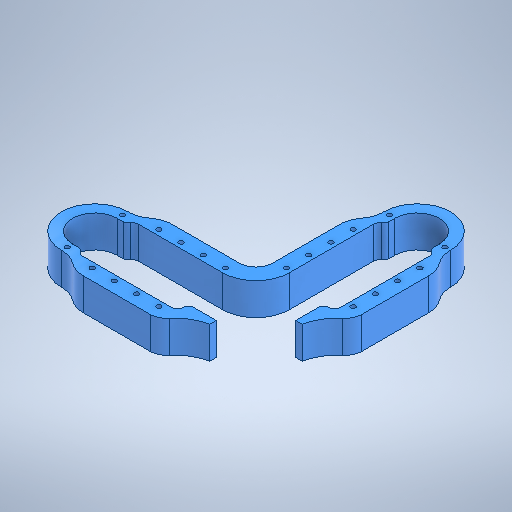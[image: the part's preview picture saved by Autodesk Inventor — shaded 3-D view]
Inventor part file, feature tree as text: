
AUTODESK INVENTOR PART (.ipt)
format: ipt  version: 2025.1 (Build 291241020, 241B)  size: 746,496 bytes
history: native  units: in
note: dims shown in document units (in); Inventor stores cm internally (conversion verified against a paired STEP export)
features: extrude x7, sketch x6, projected_geometry x5, fillet x4
ambient origin geometry x8: Origin, YZ Plane, XZ Plane, XY Plane, X Axis, Y Axis, Z Axis, Center Point
bodies: Solid1 (feature_tree)
feature tree (22):
  sketch  "Sketch1"  dims[d1=1.5in d2=1.5in d3=1.0in d4=1.0in d6=0.75in]
  extrude  "Extrusion1"  Depth=1.5in
  fillet  "Fillet1"  Radius=1.0in
  fillet  "Fillet2"  Radius=1.0in
  fillet  "Fillet4"  Radius=0.75in
  extrude  "Extrusion2"  Depth=0.75in
  fillet  "Fillet5"  Radius=1.0in
  extrude  "Extrusion3"  Depth=4.0in
  extrude  "Extrusion4"  Depth=0.75in
  extrude  "Extrusion5"  Depth=0.5in
  extrude  "Extrusion6"  Depth=0.25in
  extrude  "Extrusion7"  Depth=0.25in
  sketch  "Sketch2"  dims[d7=0.75in d8=0.75in d9=1.0in]
  projected_geometry  "Projected Loop1"
  sketch  "Sketch3"  dims[d10=4.0in d11=4.0in]
  projected_geometry  "Projected Loop2"
  sketch  "Sketch4"  dims[d17=0.75in d18=0.75in]
  projected_geometry  "Projected Loop3"
  sketch  "Sketch5"  dims[d19=0.5in d23=0.5in]
  projected_geometry  "Projected Loop4"
  sketch  "Sketch6"  dims[d24=0.75in d25=0.75in d30=0.5in d33=0.25in d47=0.75in d48=0.75in d49=0.5in d50=0.5in d51=1.0in d52=4.875in d53=5.2441in d54=5.2441in d55=0.4522in d56=0.4522in d57=2.0in d58=4.875in d59=2.0in d60=4.5in d61=4.5in d62=0.5in d63=0.5in d64=0.75in d65=0.75in d66=0.5in d70=4.9941in d71=1.355in d72=0.0in d73=2.0in d74=0.75in d76=1.5in d77=1.355in d78=0.0in d79=0.25in d80=0.2087in d81=1.0in d82=1.0in d83=1.0in d84=1.0in d85=1.0in d86=1.0in d87=1.0in d88=1.0in d89=1.0in d90=1.0in d91=1.0in d92=1.0in d93=1.25in d94=1.25in d95=1.25in d96=1.25in d97=3.0in d98=1.5in d99=3.0in d100=1.5in d101=1.375in d102=1.375in d103=1.375in d104=1.375in d105=0.0in d106=0.0in d108=1.2584in d109=1.2584in d110=0.0in d111=0.0in d112=0.025in d113=0.0in d114=0.06in d115=0.0in d116=2.625in d117=0.0in]
  projected_geometry  "Projected Loop5"
